# Revit family: 4070742+4070746 Feilo Sylvania Lighting Fixture CURSUS 306MM 218LM OVAL LED 4K with CONTINUOUS WALL HOUSING
name_source: partatom
category: Lighting Fixtures
revit_build: Autodesk Revit 2017 (Build: 20190507_1515(x64)
units: mm (PartAtom-declared; Revit-internal decimal feet)

## family parameters
Cut with Voids When Loaded = Yes
Host = Face
Light Source = Yes
OmniClass Number = 23.80.70.14
OmniClass Title = Luminaries for External Lighting
Part Type = Normal
Room Calculation Point = No
Round Connector Dimension = Use Diameter
Shared = Yes

## types (1)
- 4070742 CURSUS 306MM 218LM OVAL LED 4K
    AccessoryMaterial = Diffuser-Sylvania-Glow
    Apparent Load = 5 VA
    Assembly Code = D5020200
    AssetType = Fixed
    BodyMaterial = Body-Sylvania-Gray
    ClassificationName = Uniclass2015
    ClassificationValue = EF_70_80
    Color Filter = 16777215
    Cost = 0 $
    Default Elevation = 1219 mm
    Description = LED Exterior Lighting Recessed Surface Mounted Linear Fixture, Natural anodised extruded aluminium structure. Die-cast aluminium end caps. Installation kit with harmonic steel springs., 218 lm, 4,5W,  48lm/W, 4000K, CRI80+,non dimmable,IP67, IK07, (HxWxD) 306x50x30mm, 3 step Mac Adam Ellipse, 0.6kg,, Classe III, 21-25V-DC, energy class : A++, A+, A
    DiffuserMaterial = Diffuser-Sylvania-Glow
    Dimming Lamp Color Temperature Shift = <None>
    DocumentationLiterature = http://www.sylvania-lighting.com
    DurationUnit = hours
    ElectricShockClassification = Class III
    Emit Shape Visible in Rendering = No
    Emit from Rectangle Length = 307 mm  [stored 1.00722 ft]
    Emit from Rectangle Width = 30 mm
    ExpectedLife = 50000
    IfcExportAs = IfcLightFixtureType
    IfcExportType = IfcLightFixtureType
    ImpactProtectionIndex = IK07
    IngressProtection = IP67
    InputVoltage = 24V DC
    Keynote = 16500
    Lamp = LED
    LampColourRenderingIndex = 80
    LampColourTemperature = 4000 K
    LampNominalLuminous = 218 lm
    LampsType = LED
    Length_FEILO = 312 mm  [stored 1.02362 ft]
    LightOutputRatio = 100
    LuminousEfficacy = 48.44 lm/W
    Manufacturer = Feilo Sylvania
    ManufacturerName = Feilo Sylvania
    Material = natural anodised extruded aluminium structure housing, optical system with pmma lenses diffuser
    Model = CURSUS 306MM 218LM OVAL LED 4K
    ModelNumber = 4070742
    ModelReference = CURSUS 306MM 218LM OVAL LED 4K
    Name = CURSUS 306MM 218LM OVAL LED 4K
    NominalDepth = 30 mm
    NominalHeight = 50 mm
    NominalLength = 306 mm
    Photometric Web File = 4070742.ies
    PowerConsumption = 4.5 W
    PowerFactor = 0
    ReflectorMaterial = <By Category>
    Tilt Angle = -90.00°
    Type Image = <None>
    TypeName = CURSUS 306MM 218LM OVAL LED 4K
    URL = http://www.sylvania-lighting.com
    Voltage = 24 V
    WallThickness_FEILO = 3 mm  [stored 0.00984252 ft]
    Weight = 0.6 kg
    Width_FEILO = 35 mm

note: [stored X ft] marks values corroborated as IEEE doubles in the binary element streams (Revit-internal decimal feet)

## geometry (parser evidence)
native form markers: Sweep x1
no freeform markers — native parametric forms only
